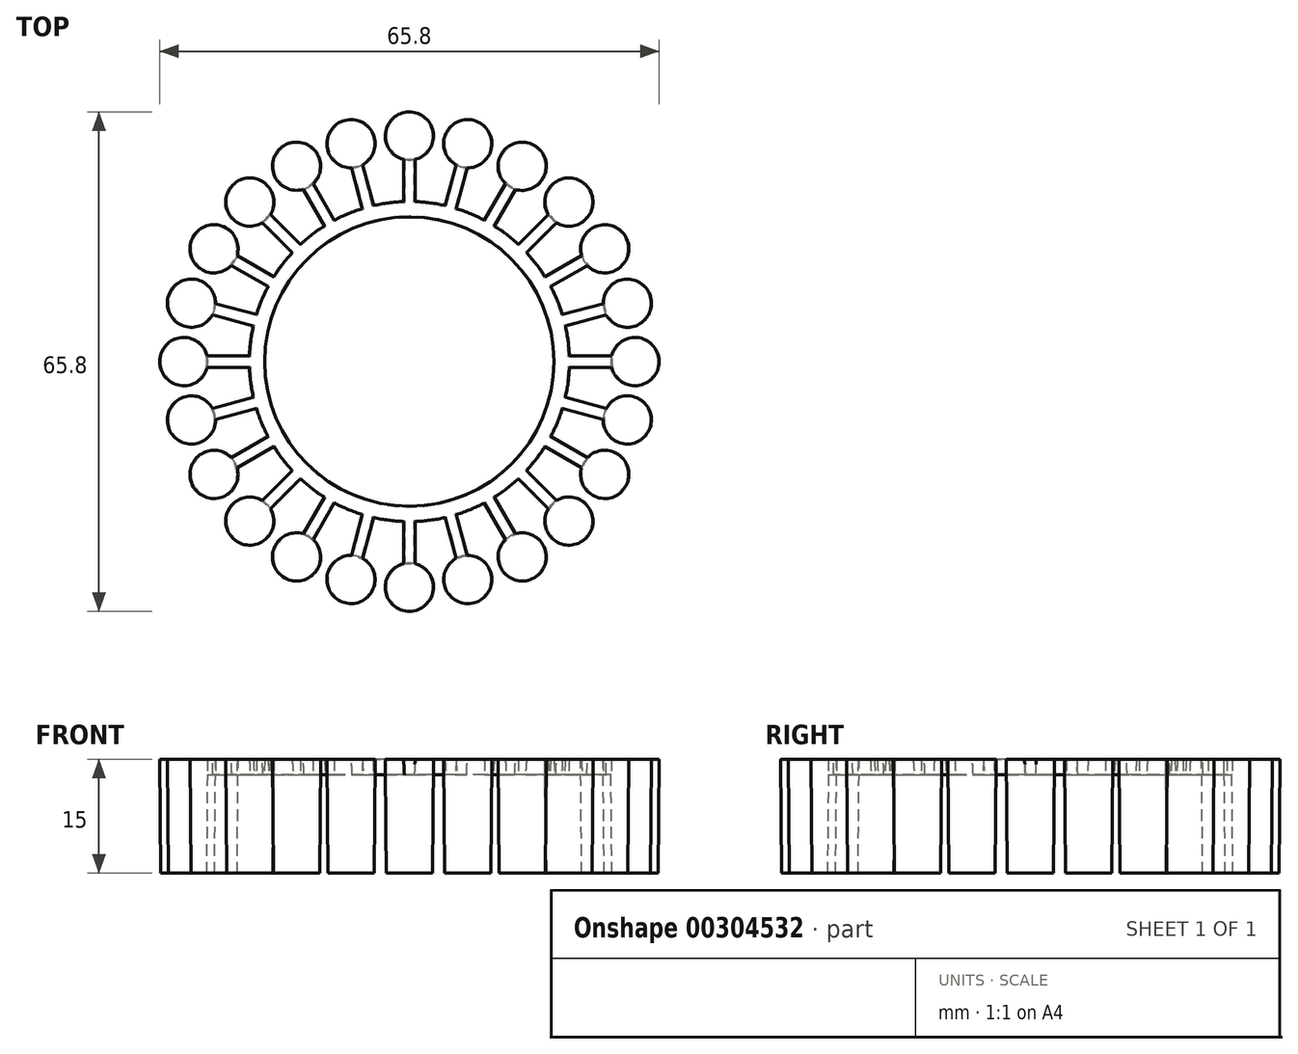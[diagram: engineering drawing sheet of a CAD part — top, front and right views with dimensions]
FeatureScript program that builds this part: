
annotation { "Feature Type Name" : "Feature", "Feature Type Description" : "" }
export const myFeature = defineFeature(function(context is Context, id is Id, definition is map)
    precondition{}
    {
        {
            var Q0;
            Q0=qCreatedBy(makeId("Top.planeOp"),FACE);
            var sketch = newSketch(context, id + "F0", { "sketchPlane" : qUnion([Q0])});
            skCircle(sketch, "E0", {"center": v(0, 29.72) * mm, "radius": 3.05 * mm});
            skLineSegment(sketch, "E1", {"start": v(0, 0) * mm, "end": v(0, 48.4) * mm, "construction": true});
            skSolve(sketch);
        }
        {
            var Q0;
            Q0 = qSketchRegion(id + "F0", true);
            extrude(context, id + "F1", {"entities" : qUnion([Q0]), "depth" : 15 * mm, "hasDraft" : true, "draftAngle" : .5 * degree});
        }
        {
            var Q0;
            Q0=qCreatedBy(makeId("Right.planeOp"),FACE);
            var sketch = newSketch(context, id + "F2", { "sketchPlane" : qUnion([Q0])});
            skLineSegment(sketch, "E2", {"start": v(0, -44.84) * mm, "end": v(0, 60.13) * mm, "construction": true});
            skSolve(sketch);
        }
        {
            var Q0;
            Q0=makeQuery(id+"F1.opExtrude","CAP_FACE",FACE,{"disambiguationData":[OSD([sQuery(id+"F0.wireOp",EDGE,"E0")])],"isStart":false});
            var sketch = newSketch(context, id + "F3", { "sketchPlane" : qUnion([Q0])});
            skLineSegment(sketch, "E3", {"start": v(0, 29.72) * mm, "end": v(0, -24.56) * mm, "construction": true});
            skLineSegment(sketch, "E4.0", {"start": v(-0.76, 27.18) * mm, "end": v(-0.76, 20.32) * mm});
            skLineSegment(sketch, "E5.0", {"start": v(0.76, 27.18) * mm, "end": v(0.76, 20.32) * mm});
            skLineSegment(sketch, "E6", {"start": v(-0.76, 27.18) * mm, "end": v(0.76, 27.18) * mm});
            skLineSegment(sketch, "E7", {"start": v(-0.76, 20.32) * mm, "end": v(0.76, 20.32) * mm});
            skSolve(sketch);
        }
        {
            var Q0;
            Q0 = qSketchRegion(id + "F3", true);
            extrude(context, id + "F4", {"entities" : qUnion([Q0]), "operationType" : NewBodyOperationType.ADD, "oppositeDirection" : true, "depth" : 2 * mm, "hasDraft" : true, "draftAngle" : 3 * degree, "draftPullDirection" : true});
        }
        {
            var Q0;
            Q0=makeQuery(id+"F1.opExtrude","SWEPT_BODY",BODY,{"disambiguationData":[OSD([sQuery(id+"F0.wireOp",EDGE,"E0")])]});
            var Q1;
            Q1=sQuery(id+"F2.wireOp",EDGE,"E2");
            circularPattern(context, id + "F5", {"operationType" : NewBodyOperationType.ADD, "entities" : qUnion([Q0]), "axis" : qUnion([Q1]), "angle" : 360 * degree, "instanceCount" : 24, "equalSpace" : true});
        }
        {
            var Q0;
            Q0=makeQuery(id+"F4.boolean.opBoolean","MERGE",FACE,{"derivedFrom":[makeQuery(id+"F1.opExtrude","CAP_FACE",FACE,{"disambiguationData":[OSD([sQuery(id+"F0.wireOp",EDGE,"E0")])],"isStart":false}),makeQuery(id+"F4.opExtrude","CAP_FACE",FACE,{"disambiguationData":[OSD([sQuery(id+"F3.wireOp",EDGE,"E4.0"),sQuery(id+"F3.wireOp",EDGE,"E5.0"),sQuery(id+"F3.wireOp",EDGE,"E6"),sQuery(id+"F3.wireOp",EDGE,"E7")])],"isStart":true})]});
            var sketch = newSketch(context, id + "F6", { "sketchPlane" : qUnion([Q0])});
            skCircle(sketch, "E8", {"center": v(0, 0) * mm, "radius": 19.05 * mm});
            skCircle(sketch, "E9.0", {"center": v(0, 0) * mm, "radius": 21.08 * mm});
            skSolve(sketch);
        }
        {
            var Q0;
            Q0 = qSketchRegion(id + "F6", true);
            extrude(context, id + "F7", {"entities" : qUnion([Q0]), "operationType" : NewBodyOperationType.ADD, "oppositeDirection" : true, "depth" : 2 * mm, "hasDraft" : true, "draftAngle" : 3 * degree, "draftPullDirection" : true});
        }
    });
